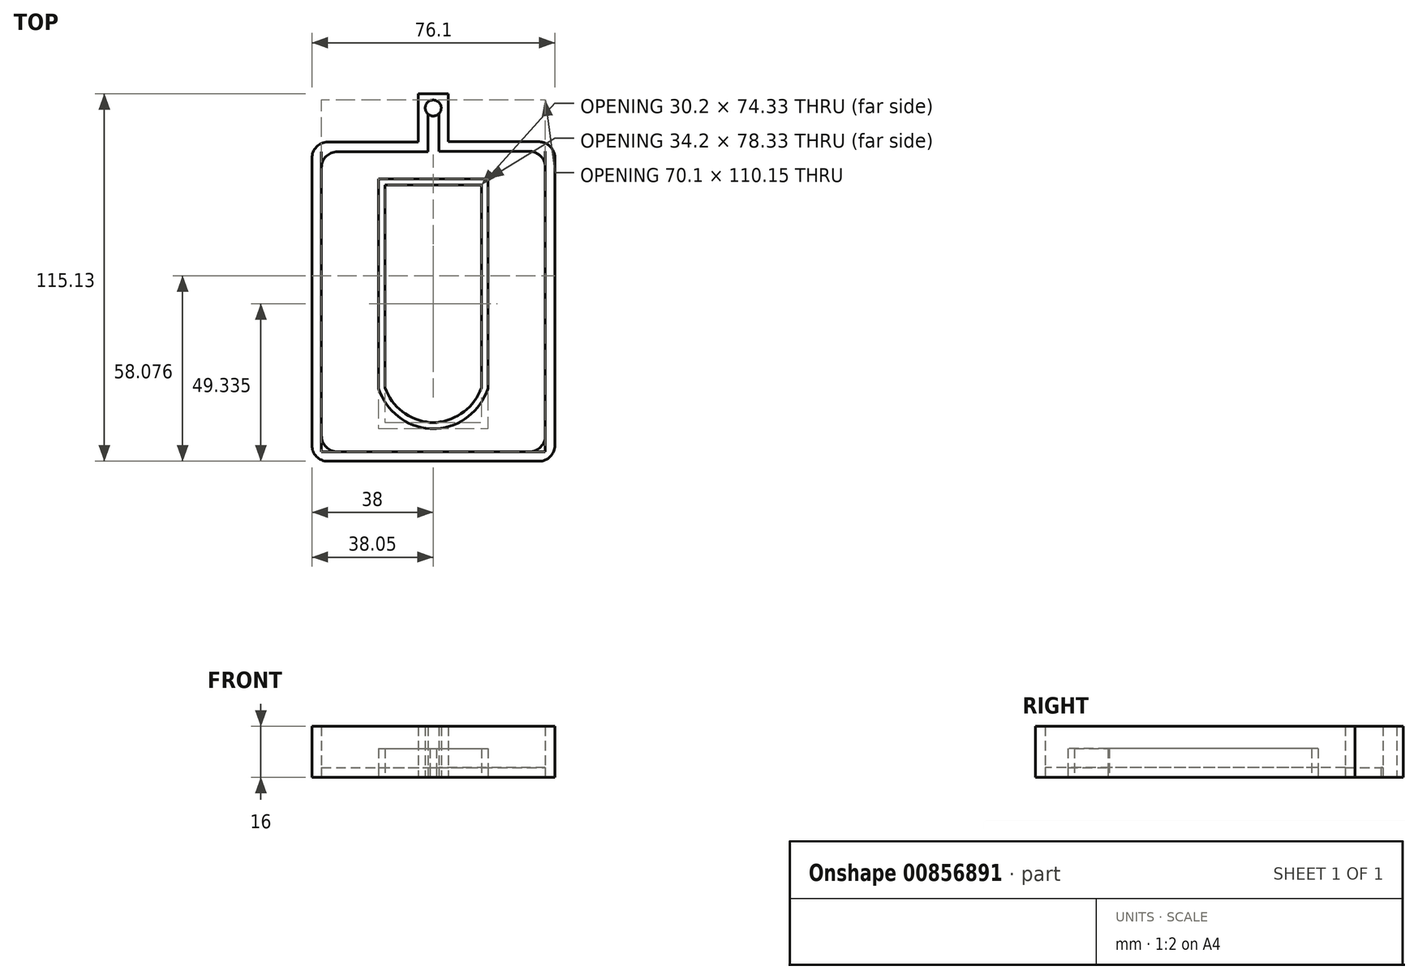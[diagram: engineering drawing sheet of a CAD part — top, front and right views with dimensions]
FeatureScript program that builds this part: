
annotation { "Feature Type Name" : "Feature", "Feature Type Description" : "" }
export const myFeature = defineFeature(function(context is Context, id is Id, definition is map)
    precondition{}
    {
        {
            var Q0;
            Q0=qCreatedBy(makeId("Top.planeOp"),FACE);
            var sketch = newSketch(context, id + "F0", { "sketchPlane" : qUnion([Q0])});
            skPoint(sketch, "E0.middle", {"position": v(0, 0) * mm});
            skLineSegment(sketch, "E1.bottom", {"start": v(-17.1, 39) * mm, "end": v(17.1, 39) * mm});
            skArc(sketch, "E2", {"start": v(-17.1, -26.78) * mm, "mid": v(-10.97, -35.48) * mm, "end": v(-1.05, -39.33) * mm});
            skArc(sketch, "E3.MirrorCS", {"start": v(17.1, -26.78) * mm, "mid": v(10.97, -35.48) * mm, "end": v(1.05, -39.33) * mm});
            skLineSegment(sketch, "E4", {"start": v(17.1, 39) * mm, "end": v(17.1, -26.78) * mm});
            skLineSegment(sketch, "E5", {"start": v(-17.1, 39) * mm, "end": v(-17.1, -26.78) * mm});
            skCircle(sketch, "E6", {"center": v(0, 61.15) * mm, "radius": 2.5 * mm});
            skLineSegment(sketch, "E7.0", {"start": v(-38, -49.5) * mm, "end": v(38.1, -49.5) * mm});
            skLineSegment(sketch, "E7.1", {"start": v(-38, 50.47) * mm, "end": v(-38, -49.5) * mm});
            skLineSegment(sketch, "E7.2", {"start": v(38.1, 50.58) * mm, "end": v(38.1, -49.5) * mm});
            skLineSegment(sketch, "E8.right", {"start": v(-4.66, 50.47) * mm, "end": v(-4.66, 65.63) * mm});
            skLineSegment(sketch, "E9.MirrorCS", {"start": v(4.76, 50.57) * mm, "end": v(4.76, 65.63) * mm});
            skLineSegment(sketch, "E10", {"start": v(-4.66, 65.63) * mm, "end": v(4.76, 65.63) * mm});
            skLineSegment(sketch, "E11", {"start": v(-38, 50.47) * mm, "end": v(-4.66, 50.47) * mm});
            skLineSegment(sketch, "E12", {"start": v(38.1, 50.58) * mm, "end": v(4.76, 50.57) * mm});
            skLineSegment(sketch, "E13.0", {"start": v(-35, 47.47) * mm, "end": v(-35, -46.5) * mm});
            skLineSegment(sketch, "E13.1", {"start": v(-35, -46.5) * mm, "end": v(35.1, -46.5) * mm});
            skLineSegment(sketch, "E13.2", {"start": v(-35, 47.47) * mm, "end": v(-1.66, 47.48) * mm});
            skLineSegment(sketch, "E13.3", {"start": v(35.1, 47.58) * mm, "end": v(35.1, -46.5) * mm});
            skLineSegment(sketch, "E13.4", {"start": v(-1.66, 47.48) * mm, "end": v(-1.66, 62.63) * mm});
            skLineSegment(sketch, "E13.5", {"start": v(-1.66, 62.63) * mm, "end": v(1.76, 62.63) * mm});
            skLineSegment(sketch, "E13.6", {"start": v(1.76, 47.57) * mm, "end": v(1.76, 62.63) * mm});
            skLineSegment(sketch, "E13.7", {"start": v(35.1, 47.58) * mm, "end": v(1.76, 47.57) * mm});
            skLineSegment(sketch, "E14", {"start": v(-1.05, -39.33) * mm, "end": v(1.05, -39.33) * mm});
            skLineSegment(sketch, "E15.0", {"start": v(-15.1, 37) * mm, "end": v(15.1, 37) * mm});
            skArc(sketch, "E15.1", {"start": v(-15.1, -26.44) * mm, "mid": v(-9.64, -33.97) * mm, "end": v(-0.97, -37.33) * mm});
            skLineSegment(sketch, "E15.2", {"start": v(-0.97, -37.33) * mm, "end": v(0.97, -37.33) * mm});
            skLineSegment(sketch, "E15.3", {"start": v(-15.1, 37) * mm, "end": v(-15.1, -26.44) * mm});
            skArc(sketch, "E15.4", {"start": v(15.1, -26.44) * mm, "mid": v(9.64, -33.97) * mm, "end": v(0.97, -37.33) * mm});
            skLineSegment(sketch, "E15.5", {"start": v(15.1, 37) * mm, "end": v(15.1, -26.44) * mm});
            skSolve(sketch);
        }
        {
            var Q0;
            Q0=makeQuery(id+"F0.imprint","IMPRINT",FACE,{"disambiguationData":[TD([[makeQuery(id+"F0.imprint","IMPRINT",EDGE,{"derivedFrom":sQuery(id+"F0.wireOp",EDGE,"E7.0")}),1.0]])]});
            extrude(context, id + "F1", {"entities" : qUnion([Q0]), "depth" : 16 * mm, "offsetDistance" : 25 * mm});
        }
        {
            var Q0;
            Q0=makeQuery(id+"F0.imprint","IMPRINT",FACE,{"disambiguationData":[TD([[makeQuery(id+"F0.imprint","IMPRINT",EDGE,{"derivedFrom":sQuery(id+"F0.wireOp",EDGE,"E1.bottom")}),-1.0]])]});
            extrude(context, id + "F2", {"entities" : qUnion([Q0]), "depth" : 9 * mm, "offsetDistance" : 25 * mm});
        }
        {
            var Q0;
            Q0=makeQuery(id+"F0.imprint","IMPRINT",FACE,{"disambiguationData":[TD([[makeQuery(id+"F0.imprint","IMPRINT",EDGE,{"derivedFrom":sQuery(id+"F0.wireOp",EDGE,"E1.bottom")}),1.0]])]});
            extrude(context, id + "F3", {"entities" : qUnion([Q0]), "depth" : 3 * mm, "offsetDistance" : 25 * mm});
        }
        {
            var Q0;
            Q0=makeQuery(id+"F1.opExtrude","SWEPT_EDGE",EDGE,{"disambiguationData":[OSD([sQuery(id+"F0.wireOp",EDGE,"E7.1"),sQuery(id+"F0.wireOp",EDGE,"E11")])]});
            var Q1;
            Q1=makeQuery(id+"F1.opExtrude","SWEPT_EDGE",EDGE,{"disambiguationData":[OSD([sQuery(id+"F0.wireOp",EDGE,"E7.0"),sQuery(id+"F0.wireOp",EDGE,"E7.1")])]});
            var Q2;
            Q2=makeQuery(id+"F1.opExtrude","SWEPT_EDGE",EDGE,{"disambiguationData":[OSD([sQuery(id+"F0.wireOp",EDGE,"E7.0"),sQuery(id+"F0.wireOp",EDGE,"E7.2")])]});
            var Q3;
            Q3=makeQuery(id+"F1.opExtrude","SWEPT_EDGE",EDGE,{"disambiguationData":[OSD([sQuery(id+"F0.wireOp",EDGE,"E7.2"),sQuery(id+"F0.wireOp",EDGE,"E12")])]});
            var Q4;
            Q4=makeQuery(id+"F1.opExtrude","SWEPT_EDGE",EDGE,{"disambiguationData":[OSD([sQuery(id+"F0.wireOp",EDGE,"E13.3"),sQuery(id+"F0.wireOp",EDGE,"E13.7")])]});
            var Q5;
            Q5=makeQuery(id+"F1.opExtrude","SWEPT_EDGE",EDGE,{"disambiguationData":[OSD([sQuery(id+"F0.wireOp",EDGE,"E13.0"),sQuery(id+"F0.wireOp",EDGE,"E13.2")])]});
            var Q6;
            Q6=makeQuery(id+"F1.opExtrude","SWEPT_EDGE",EDGE,{"disambiguationData":[OSD([sQuery(id+"F0.wireOp",EDGE,"E13.1"),sQuery(id+"F0.wireOp",EDGE,"E13.3")])]});
            var Q7;
            Q7=makeQuery(id+"F1.opExtrude","SWEPT_EDGE",EDGE,{"disambiguationData":[OSD([sQuery(id+"F0.wireOp",EDGE,"E13.0"),sQuery(id+"F0.wireOp",EDGE,"E13.1")])]});
            fillet(context, id + "F4", {"entities" : qUnion([Q0, Q1, Q2, Q3, Q4, Q5, Q6, Q7]), "radius" : 5 * mm, "tangentPropagation" : true, "allowEdgeOverflow" : false});
        }
    });
